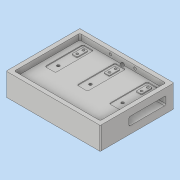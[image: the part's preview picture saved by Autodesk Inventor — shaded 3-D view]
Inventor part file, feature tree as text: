
AUTODESK INVENTOR PART (.ipt)
format: ipt  version: 2018 (Build 220112000, 112)  size: 468,480 bytes
history: native  units: mm
features: sketch x15, projected_geometry x14, extrude x8, hole x7, fillet x5, plane x1, mirror x1
ambient origin geometry x8: Origin, YZ Plane, XZ Plane, XY Plane, X Axis, Y Axis, Z Axis, Center Point
bodies: Volumenkörper1 (feature_tree)
feature tree (51):
  extrude  "Extrusion1"  Depth=180.0mm
  extrude  "Extrusion2"  Depth=10.0mm
  extrude  "Extrusion3"  Depth=27.0mm
  hole  "Bohrung1"  [1 undecoded]
  extrude  "Extrusion4"  Depth=20.0mm
  extrude  "Extrusion5"  Depth=65.5mm
  hole  "Bohrung2"  [1 undecoded]
  hole  "Bohrung3"  [1 undecoded]
  hole  "Bohrung4"  [1 undecoded]
  hole  "Bohrung5"  [1 undecoded]
  extrude  "Extrusion6"  Depth=2.0mm
  extrude  "Extrusion7"  Depth=6.5mm
  fillet  "Rundung3"  Radius=6.5mm
  plane  "Arbeitsebene1"
  mirror  "Spiegeln1"
  hole  "Bohrung6"  [1 undecoded]
  extrude  "Extrusion8"  Depth=6.5mm
  hole  "Bohrung7"  [1 undecoded]
  fillet  "Rundung2"  Radius=93.0mm
  fillet  "Rundung1"  Radius=93.0mm
  fillet  "Rundung4"  Radius=3.5mm
  fillet  "Rundung5"  Radius=20.0mm
  sketch  "Skizze1"  dims[d0=230.0mm d1=180.0mm]
  sketch  "Skizze2"  dims[d2=39.0mm d3=0.0mm d4=10.0mm]
  projected_geometry  "Projizierte Kontur1"
  sketch  "Skizze3"  dims[d5=16.0mm d6=0.0mm d7=27.0mm]
  sketch  "Skizze4"  dims[d8=13.0mm d9=27.0mm d10=13.0mm]
  projected_geometry  "Projizierte Kontur2"
  projected_geometry  "Projizierte Kontur3"
  projected_geometry  "Projizierte Kontur4"
  projected_geometry  "Projizierte Kontur5"
  sketch  "Skizze5"  dims[d11=27.0mm d12=13.0mm d13=20.0mm]
  projected_geometry  "Projizierte Kontur6"
  sketch  "Skizze6"  dims[d14=20.0mm d15=65.5mm]
  projected_geometry  "Projizierte Kontur7"
  sketch  "Skizze7"  dims[d16=65.5mm d17=12.5mm]
  projected_geometry  "Projizierte Kontur8"
  sketch  "Skizze8"  dims[d18=2.0mm d19=0.0mm d20=15.0mm]
  projected_geometry  "Projizierte Kontur9"
  sketch  "Skizze9"  dims[d21=5.0mm]
  sketch  "Skizze10"  dims[d22=5.5mm d23=6.0mm d24=4.0mm d25=2.0mm d26=90.0deg d27=8.0mm d28=20.594885mm d29=5.0mm]
  projected_geometry  "Projizierte Kontur10"
  projected_geometry  "Projizierte Kontur11"
  projected_geometry  "Projizierte Kontur12"
  sketch  "Skizze11"  dims[d30=15.0mm d31=5.0mm]
  projected_geometry  "Projizierte Kontur13"
  sketch  "Skizze12"  dims[d32=15.0mm d33=2.0mm]
  sketch  "Skizze13"  dims[d34=6.5mm d35=6.5mm d36=6.5mm]
  sketch  "Skizze14"  dims[d37=6.5mm d38=6.5mm]
  sketch  "Skizze15"  dims[d39=6.5mm d40=6.5mm d41=93.0mm d42=93.0mm d43=93.0mm d44=93.0mm d45=3.5mm d46=20.0mm d47=10.0mm d48=0.0mm d49=9.0mm d50=9.0mm d51=9.0mm d52=9.0mm d53=9.0mm d54=9.0mm d55=5.5mm d56=0.0mm d57=6.5mm d58=2.0mm d59=14.0mm d60=10.0mm d61=6.0mm d62=4.0mm d63=2.0mm d64=90.0deg d65=12.0mm d66=20.594885mm d67=10.0mm d68=10.0mm d69=6.647mm d70=25.0mm d71=4.0mm d72=2.0mm d73=90.0deg d74=30.0mm d75=20.594885mm d76=15.0mm d77=15.0mm d78=15.0mm d79=6.647mm d80=15.0mm d81=4.0mm d82=2.0mm d83=90.0deg d84=20.0mm d85=20.594885mm d86=20.0mm d87=6.647mm d88=16.0mm d89=4.0mm d90=2.0mm d91=90.0deg d92=22.2mm d93=20.594885mm d94=20.0mm d97=10.0mm d98=0.0mm d99=90.0mm d100=20.0mm d101=20.0mm d102=70.0mm d103=18.0mm d104=17.0mm d105=25.0mm d106=0.0mm d107=3.1mm d108=-115.0mm d109=60.0mm d110=7.0mm d111=7.0mm d112=6.5mm d113=12.0mm d114=4.0mm d115=2.0mm d116=90.0deg d117=17.1mm d118=20.594885mm d119=16.0mm d120=16.0mm d121=60.0mm d122=40.0mm d123=4.0mm d124=0.0mm d125=60.0mm d126=7.0mm d127=6.5mm d128=12.0mm d129=4.0mm d130=2.0mm d131=90.0deg d132=17.1mm d133=20.594885mm d134=3.1mm d136=4.0mm]
  projected_geometry  "Projizierte Kontur14"
note: 7 required parameter values undecoded (feature->parameter linkage not recoverable at this tier; creation-order binding heuristic only, values carry confidence <= 0.55)
